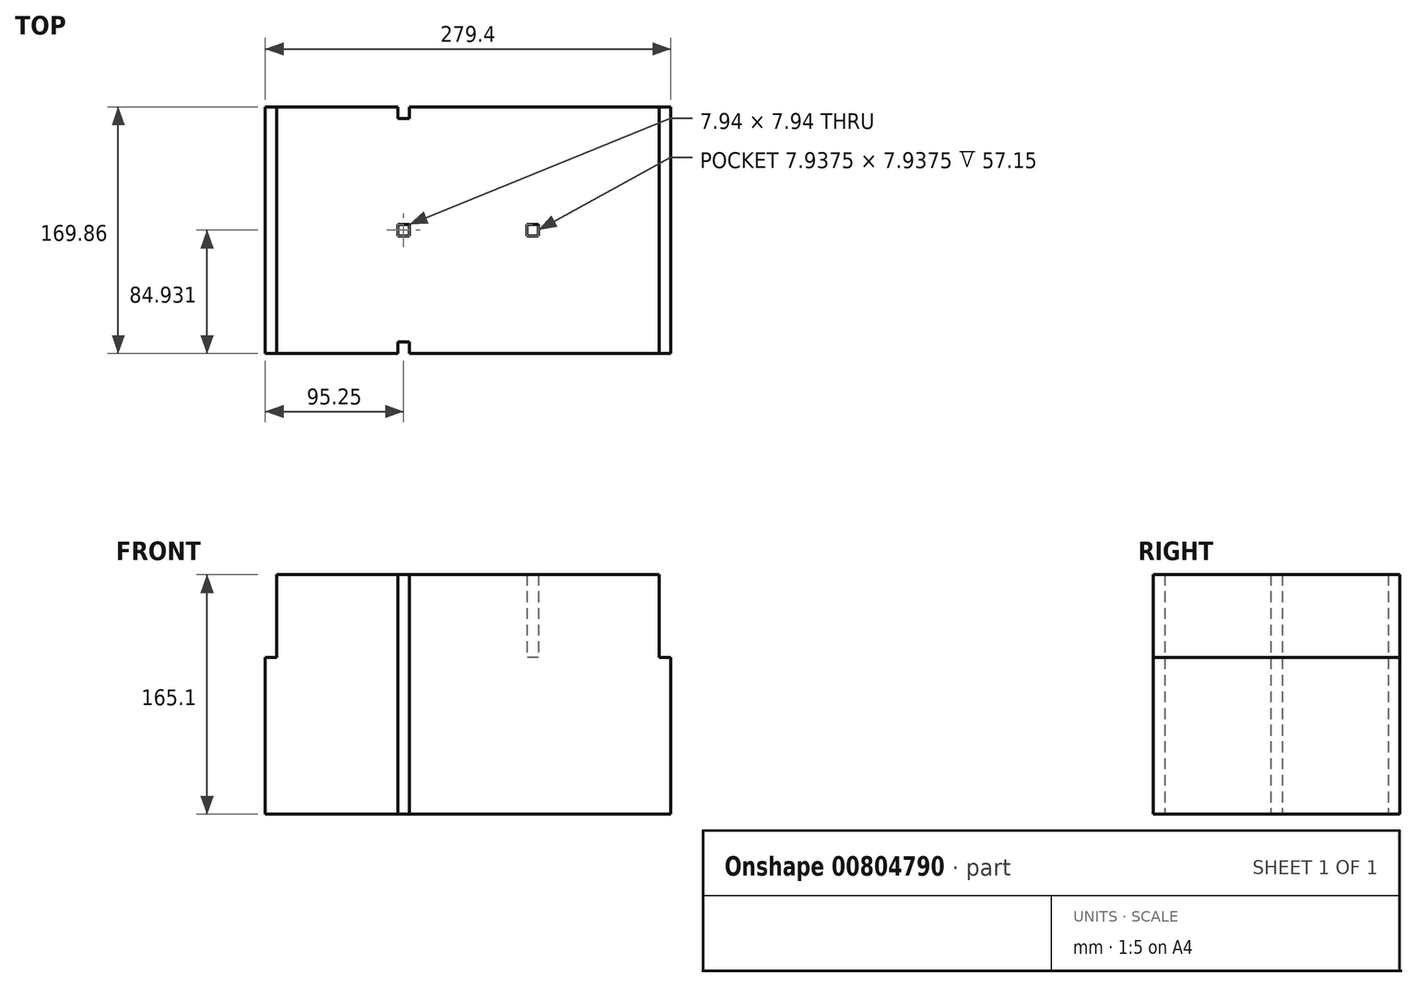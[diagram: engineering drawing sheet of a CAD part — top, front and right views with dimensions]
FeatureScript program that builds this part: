
annotation { "Feature Type Name" : "Feature", "Feature Type Description" : "" }
export const myFeature = defineFeature(function(context is Context, id is Id, definition is map)
    precondition{}
    {
        {
            var Q0;
            Q0=qCreatedBy(makeId("Top.planeOp"),FACE);
            var sketch = newSketch(context, id + "F0", { "sketchPlane" : qUnion([Q0])});
            skLineSegment(sketch, "E0.bottom", {"start": v(-139.7, 0) * mm, "end": v(-44.45, 0) * mm});
            skLineSegment(sketch, "E0.top", {"start": v(-139.7, 88.9) * mm, "end": v(-44.45, 88.9) * mm});
            skLineSegment(sketch, "E0.left", {"start": v(-139.7, 0) * mm, "end": v(-139.7, 88.9) * mm});
            skLineSegment(sketch, "E1.bottom", {"start": v(-44.45, 88.9) * mm, "end": v(44.45, 88.9) * mm});
            skLineSegment(sketch, "E1.top", {"start": v(-44.45, 0) * mm, "end": v(44.45, 0) * mm});
            skLineSegment(sketch, "E2.bottom", {"start": v(44.45, 88.9) * mm, "end": v(139.7, 88.9) * mm});
            skLineSegment(sketch, "E2.top", {"start": v(44.45, 0) * mm, "end": v(139.7, 0) * mm});
            skLineSegment(sketch, "E2.right", {"start": v(139.7, 88.9) * mm, "end": v(139.7, 0) * mm});
            skLineSegment(sketch, "E3", {"start": v(131.76, 88.9) * mm, "end": v(131.76, 0) * mm});
            skLineSegment(sketch, "E4", {"start": v(-131.76, 88.9) * mm, "end": v(-131.76, 0) * mm});
            skLineSegment(sketch, "E5", {"start": v(48.42, 0) * mm, "end": v(48.42, 88.9) * mm});
            skLineSegment(sketch, "E6", {"start": v(-40.48, 88.9) * mm, "end": v(-40.48, 0) * mm});
            skLineSegment(sketch, "E7", {"start": v(-48.42, 88.9) * mm, "end": v(-48.42, 0) * mm});
            skLineSegment(sketch, "E8", {"start": v(40.48, 88.9) * mm, "end": v(40.48, 0) * mm});
            skLineSegment(sketch, "E9.bottom", {"start": v(-139.7, 0) * mm, "end": v(-139.7, 0) * mm});
            skLineSegment(sketch, "E9.top", {"start": v(-139.7, 5.35) * mm, "end": v(-139.7, 5.35) * mm});
            skLineSegment(sketch, "E9.left", {"start": v(-139.7, 0) * mm, "end": v(-139.7, 5.35) * mm});
            skLineSegment(sketch, "E9.right", {"start": v(-139.7, 0) * mm, "end": v(-139.7, 5.35) * mm});
            skLineSegment(sketch, "E10.bottom", {"start": v(139.7, 0) * mm, "end": v(139.7, 0) * mm});
            skLineSegment(sketch, "E10.top", {"start": v(139.7, 7.94) * mm, "end": v(139.7, 7.94) * mm});
            skLineSegment(sketch, "E10.left", {"start": v(139.7, 0) * mm, "end": v(139.7, 7.94) * mm});
            skLineSegment(sketch, "E10.right", {"start": v(139.7, 0) * mm, "end": v(139.7, 7.94) * mm});
            skLineSegment(sketch, "E11.left", {"start": v(139.7, 7.94) * mm, "end": v(139.7, 0) * mm});
            skLineSegment(sketch, "E11.right", {"start": v(139.7, 7.94) * mm, "end": v(139.7, 0) * mm});
            skLineSegment(sketch, "E12.bottom", {"start": v(-139.7, 0) * mm, "end": v(139.7, 0) * mm});
            skLineSegment(sketch, "E12.top", {"start": v(-139.7, 7.94) * mm, "end": v(139.7, 7.94) * mm});
            skLineSegment(sketch, "E12.left", {"start": v(-139.7, 0) * mm, "end": v(-139.7, 7.94) * mm});
            skLineSegment(sketch, "E13.bottom", {"start": v(139.7, 88.9) * mm, "end": v(-139.7, 88.9) * mm});
            skLineSegment(sketch, "E13.top", {"start": v(139.7, 80.96) * mm, "end": v(-139.7, 80.96) * mm});
            skLineSegment(sketch, "E13.left", {"start": v(139.7, 88.9) * mm, "end": v(139.7, 80.96) * mm});
            skLineSegment(sketch, "E13.right", {"start": v(-139.7, 88.9) * mm, "end": v(-139.7, 80.96) * mm});
            skSolve(sketch);
        }
        {
            var Q0;
            {var subQ0=sQuery(id+"F0.wireOp",EDGE,"E13.bottom");var subQ1=sQuery(id+"F0.wireOp",EDGE,"E4");var subQ2=makeQuery(id+"F0.imprint","INTERSECT",VERTEX,{"derivedFrom":[subQ1,subQ0]});Q0=makeQuery(id+"F0.imprint","IMPRINT",FACE,{"disambiguationData":[TD([[makeQuery(id+"F0.imprint","IMPRINT",EDGE,{"disambiguationData":[TD([[subQ2,-1.0]])],"derivedFrom":subQ1}),1.0]])]});}
            var Q1;
            {var subQ0=sQuery(id+"F0.wireOp",EDGE,"E13.bottom");var subQ1=sQuery(id+"F0.wireOp",EDGE,"E6");var subQ2=makeQuery(id+"F0.imprint","INTERSECT",VERTEX,{"derivedFrom":[subQ1,subQ0]});Q1=makeQuery(id+"F0.imprint","IMPRINT",FACE,{"disambiguationData":[TD([[makeQuery(id+"F0.imprint","IMPRINT",EDGE,{"disambiguationData":[TD([[subQ2,-1.0]])],"derivedFrom":subQ1}),1.0]])]});}
            var Q2;
            {var subQ0=sQuery(id+"F0.wireOp",EDGE,"E13.bottom");var subQ1=sQuery(id+"F0.wireOp",EDGE,"E6");var subQ2=makeQuery(id+"F0.imprint","INTERSECT",VERTEX,{"derivedFrom":[subQ1,subQ0]});Q2=makeQuery(id+"F0.imprint","IMPRINT",FACE,{"disambiguationData":[TD([[makeQuery(id+"F0.imprint","IMPRINT",EDGE,{"disambiguationData":[TD([[subQ2,-1.0]])],"derivedFrom":subQ1}),-1.0]])]});}
            var Q3;
            {var subQ5=sQuery(id+"F0.wireOp",EDGE,"E13.right");Q3=makeQuery(id+"F0.imprint","IMPRINT",FACE,{"disambiguationData":[TD([[makeQuery(id+"F0.imprint","IMPRINT",EDGE,{"derivedFrom":subQ5}),1.0]])]});}
            var Q4;
            {var subQ0=sQuery(id+"F0.wireOp",EDGE,"E13.bottom");var subQ1=sQuery(id+"F0.wireOp",EDGE,"E5");var subQ2=makeQuery(id+"F0.imprint","INTERSECT",VERTEX,{"derivedFrom":[subQ1,subQ0]});Q4=makeQuery(id+"F0.imprint","IMPRINT",FACE,{"disambiguationData":[TD([[makeQuery(id+"F0.imprint","IMPRINT",EDGE,{"disambiguationData":[TD([[subQ2,1.0]])],"derivedFrom":subQ1}),1.0]])]});}
            var Q5;
            {var subQ0=sQuery(id+"F0.wireOp",EDGE,"E13.bottom");var subQ1=sQuery(id+"F0.wireOp",EDGE,"E3");var subQ2=makeQuery(id+"F0.imprint","INTERSECT",VERTEX,{"derivedFrom":[subQ1,subQ0]});Q5=makeQuery(id+"F0.imprint","IMPRINT",FACE,{"disambiguationData":[TD([[makeQuery(id+"F0.imprint","IMPRINT",EDGE,{"disambiguationData":[TD([[subQ2,-1.0]])],"derivedFrom":subQ1}),-1.0]])]});}
            var Q6;
            {var subQ5=sQuery(id+"F0.wireOp",EDGE,"E13.left");Q6=makeQuery(id+"F0.imprint","IMPRINT",FACE,{"disambiguationData":[TD([[makeQuery(id+"F0.imprint","IMPRINT",EDGE,{"derivedFrom":subQ5}),-1.0]])]});}
            extrude(context, id + "F1", {"entities" : qUnion([Q0, Q1, Q2, Q3, Q4, Q5, Q6]), "depth" : 165.1 * mm, "offsetDistance" : 25.4 * mm});
        }
        {
            var Q0;
            {var subQ0=sQuery(id+"F0.wireOp",EDGE,"E13.top");var subQ1=sQuery(id+"F0.wireOp",EDGE,"E4");var subQ2=makeQuery(id+"F0.imprint","INTERSECT",VERTEX,{"derivedFrom":[subQ1,subQ0]});Q0=makeQuery(id+"F0.imprint","IMPRINT",FACE,{"disambiguationData":[TD([[makeQuery(id+"F0.imprint","IMPRINT",EDGE,{"disambiguationData":[TD([[subQ2,-1.0]])],"derivedFrom":subQ1}),1.0]])]});}
            var Q1;
            {var subQ0=sQuery(id+"F0.wireOp",EDGE,"E13.top");var subQ1=sQuery(id+"F0.wireOp",EDGE,"E6");var subQ2=makeQuery(id+"F0.imprint","INTERSECT",VERTEX,{"derivedFrom":[subQ1,subQ0]});Q1=makeQuery(id+"F0.imprint","IMPRINT",FACE,{"disambiguationData":[TD([[makeQuery(id+"F0.imprint","IMPRINT",EDGE,{"disambiguationData":[TD([[subQ2,-1.0]])],"derivedFrom":subQ1}),1.0]])]});}
            var Q2;
            {var subQ0=sQuery(id+"F0.wireOp",EDGE,"E13.top");var subQ1=sQuery(id+"F0.wireOp",EDGE,"E3");var subQ2=makeQuery(id+"F0.imprint","INTERSECT",VERTEX,{"derivedFrom":[subQ1,subQ0]});Q2=makeQuery(id+"F0.imprint","IMPRINT",FACE,{"disambiguationData":[TD([[makeQuery(id+"F0.imprint","IMPRINT",EDGE,{"disambiguationData":[TD([[subQ2,-1.0]])],"derivedFrom":subQ1}),-1.0]])]});}
            extrude(context, id + "F2", {"entities" : qUnion([Q0, Q1, Q2]), "depth" : 1.59 * mm, "offsetDistance" : 25.4 * mm});
        }
        {
            var Q0;
            {var subQ3=sQuery(id+"F0.wireOp",EDGE,"E6");Q0=makeQuery(id+"F0.imprint","IMPRINT",FACE,{"disambiguationData":[TD([[makeQuery(id+"F0.imprint","IMPRINT",EDGE,{"derivedFrom":subQ3}),-1.0]])]});}
            var Q1;
            {var subQ3=sQuery(id+"F0.wireOp",EDGE,"E5");Q1=makeQuery(id+"F0.imprint","IMPRINT",FACE,{"disambiguationData":[TD([[makeQuery(id+"F0.imprint","IMPRINT",EDGE,{"derivedFrom":subQ3}),1.0]])]});}
            var Q2;
            {var subQ0=sQuery(id+"F0.wireOp",EDGE,"E2.right");Q2=makeQuery(id+"F0.imprint","IMPRINT",FACE,{"disambiguationData":[TD([[makeQuery(id+"F0.imprint","IMPRINT",EDGE,{"derivedFrom":subQ0}),-1.0]])]});}
            var Q3;
            {var subQ0=sQuery(id+"F0.wireOp",EDGE,"E0.left");Q3=makeQuery(id+"F0.imprint","IMPRINT",FACE,{"disambiguationData":[TD([[makeQuery(id+"F0.imprint","IMPRINT",EDGE,{"derivedFrom":subQ0}),-1.0]])]});}
            var Q4;
            {var subQ0=sQuery(id+"F0.wireOp",EDGE,"E12.bottom");var subQ1=sQuery(id+"F0.wireOp",EDGE,"E4");var subQ2=makeQuery(id+"F0.imprint","INTERSECT",VERTEX,{"derivedFrom":[subQ1,subQ0]});Q4=makeQuery(id+"F0.imprint","IMPRINT",FACE,{"disambiguationData":[TD([[makeQuery(id+"F0.imprint","IMPRINT",EDGE,{"disambiguationData":[TD([[subQ2,1.0]])],"derivedFrom":subQ1}),1.0]])]});}
            var Q5;
            {var subQ0=sQuery(id+"F0.wireOp",EDGE,"E12.bottom");var subQ1=sQuery(id+"F0.wireOp",EDGE,"E4");var subQ2=makeQuery(id+"F0.imprint","INTERSECT",VERTEX,{"derivedFrom":[subQ1,subQ0]});Q5=makeQuery(id+"F0.imprint","IMPRINT",FACE,{"disambiguationData":[TD([[makeQuery(id+"F0.imprint","IMPRINT",EDGE,{"disambiguationData":[TD([[subQ2,1.0]])],"derivedFrom":subQ1}),-1.0]])]});}
            var Q6;
            {var subQ5=sQuery(id+"F0.wireOp",EDGE,"E13.right");Q6=makeQuery(id+"F0.imprint","IMPRINT",FACE,{"disambiguationData":[TD([[makeQuery(id+"F0.imprint","IMPRINT",EDGE,{"derivedFrom":subQ5}),1.0]])]});}
            var Q7;
            {var subQ0=sQuery(id+"F0.wireOp",EDGE,"E13.bottom");var subQ1=sQuery(id+"F0.wireOp",EDGE,"E4");var subQ2=makeQuery(id+"F0.imprint","INTERSECT",VERTEX,{"derivedFrom":[subQ1,subQ0]});Q7=makeQuery(id+"F0.imprint","IMPRINT",FACE,{"disambiguationData":[TD([[makeQuery(id+"F0.imprint","IMPRINT",EDGE,{"disambiguationData":[TD([[subQ2,-1.0]])],"derivedFrom":subQ1}),1.0]])]});}
            var Q8;
            {var subQ0=sQuery(id+"F0.wireOp",EDGE,"E13.bottom");var subQ1=sQuery(id+"F0.wireOp",EDGE,"E6");var subQ2=makeQuery(id+"F0.imprint","INTERSECT",VERTEX,{"derivedFrom":[subQ1,subQ0]});Q8=makeQuery(id+"F0.imprint","IMPRINT",FACE,{"disambiguationData":[TD([[makeQuery(id+"F0.imprint","IMPRINT",EDGE,{"disambiguationData":[TD([[subQ2,-1.0]])],"derivedFrom":subQ1}),1.0]])]});}
            var Q9;
            {var subQ0=sQuery(id+"F0.wireOp",EDGE,"E12.bottom");var subQ1=sQuery(id+"F0.wireOp",EDGE,"E6");var subQ2=makeQuery(id+"F0.imprint","INTERSECT",VERTEX,{"derivedFrom":[subQ1,subQ0]});Q9=makeQuery(id+"F0.imprint","IMPRINT",FACE,{"disambiguationData":[TD([[makeQuery(id+"F0.imprint","IMPRINT",EDGE,{"disambiguationData":[TD([[subQ2,1.0]])],"derivedFrom":subQ1}),1.0]])]});}
            var Q10;
            {var subQ0=sQuery(id+"F0.wireOp",EDGE,"E12.bottom");var subQ1=sQuery(id+"F0.wireOp",EDGE,"E3");var subQ2=makeQuery(id+"F0.imprint","INTERSECT",VERTEX,{"derivedFrom":[subQ1,subQ0]});Q10=makeQuery(id+"F0.imprint","IMPRINT",FACE,{"disambiguationData":[TD([[makeQuery(id+"F0.imprint","IMPRINT",EDGE,{"disambiguationData":[TD([[subQ2,1.0]])],"derivedFrom":subQ1}),-1.0]])]});}
            var Q11;
            {var subQ5=sQuery(id+"F0.wireOp",EDGE,"E10.left");Q11=makeQuery(id+"F0.imprint","IMPRINT",FACE,{"disambiguationData":[TD([[makeQuery(id+"F0.imprint","IMPRINT",EDGE,{"derivedFrom":subQ5}),1.0]])]});}
            var Q12;
            {var subQ5=sQuery(id+"F0.wireOp",EDGE,"E13.left");Q12=makeQuery(id+"F0.imprint","IMPRINT",FACE,{"disambiguationData":[TD([[makeQuery(id+"F0.imprint","IMPRINT",EDGE,{"derivedFrom":subQ5}),-1.0]])]});}
            var Q13;
            {var subQ0=sQuery(id+"F0.wireOp",EDGE,"E13.bottom");var subQ1=sQuery(id+"F0.wireOp",EDGE,"E3");var subQ2=makeQuery(id+"F0.imprint","INTERSECT",VERTEX,{"derivedFrom":[subQ1,subQ0]});Q13=makeQuery(id+"F0.imprint","IMPRINT",FACE,{"disambiguationData":[TD([[makeQuery(id+"F0.imprint","IMPRINT",EDGE,{"disambiguationData":[TD([[subQ2,-1.0]])],"derivedFrom":subQ1}),-1.0]])]});}
            extrude(context, id + "F3", {"entities" : qUnion([Q0, Q1, Q2, Q3, Q4, Q5, Q6, Q7, Q8, Q9, Q10, Q11, Q12, Q13]), "depth" : 107.95 * mm, "offsetDistance" : 25.4 * mm});
        }
        {
            var Q0;
            Q0=makeQuery(id+"F1.opExtrude","SWEPT_BODY",BODY,{"disambiguationData":[OSD([sQuery(id+"F0.wireOp",EDGE,"E13.bottom"),sQuery(id+"F0.wireOp",EDGE,"E13.top"),sQuery(id+"F0.wireOp",EDGE,"E13.left"),sQuery(id+"F0.wireOp",EDGE,"E13.right")])]});
            var Q1;
            Q1=makeQuery(id+"F2.opExtrude","SWEPT_BODY",BODY,{"disambiguationData":[OSD([sQuery(id+"F0.wireOp",EDGE,"E3"),sQuery(id+"F0.wireOp",EDGE,"E5"),sQuery(id+"F0.wireOp",EDGE,"E12.top"),sQuery(id+"F0.wireOp",EDGE,"E13.top")])]});
            var Q2;
            Q2=makeQuery(id+"F2.opExtrude","SWEPT_BODY",BODY,{"disambiguationData":[OSD([sQuery(id+"F0.wireOp",EDGE,"E4"),sQuery(id+"F0.wireOp",EDGE,"E7"),sQuery(id+"F0.wireOp",EDGE,"E12.top"),sQuery(id+"F0.wireOp",EDGE,"E13.top")])]});
            var Q3;
            Q3=makeQuery(id+"F3.opExtrude","SWEPT_BODY",BODY,{"disambiguationData":[OSD([sQuery(id+"F0.wireOp",EDGE,"E0.left"),sQuery(id+"F0.wireOp",EDGE,"E2.right"),sQuery(id+"F0.wireOp",EDGE,"E3"),sQuery(id+"F0.wireOp",EDGE,"E4"),sQuery(id+"F0.wireOp",EDGE,"E5"),sQuery(id+"F0.wireOp",EDGE,"E6"),sQuery(id+"F0.wireOp",EDGE,"E7"),sQuery(id+"F0.wireOp",EDGE,"E8"),sQuery(id+"F0.wireOp",EDGE,"E12.bottom"),sQuery(id+"F0.wireOp",EDGE,"E12.top"),sQuery(id+"F0.wireOp",EDGE,"E12.left"),sQuery(id+"F0.wireOp",EDGE,"E10.left"),sQuery(id+"F0.wireOp",EDGE,"E13.bottom"),sQuery(id+"F0.wireOp",EDGE,"E13.top"),sQuery(id+"F0.wireOp",EDGE,"E13.left"),sQuery(id+"F0.wireOp",EDGE,"E13.right")])]});
            var Q4;
            Q4=makeQuery(id+"F2.opExtrude","SWEPT_BODY",BODY,{"disambiguationData":[OSD([sQuery(id+"F0.wireOp",EDGE,"E6"),sQuery(id+"F0.wireOp",EDGE,"E8"),sQuery(id+"F0.wireOp",EDGE,"E12.top"),sQuery(id+"F0.wireOp",EDGE,"E13.top")])]});
            booleanBodies(context, id + "F4", {"operationType" : BooleanOperationType.UNION, "tools" : qUnion([Q0, Q1, Q2, Q3, Q4])});
        }
        {
            var Q0;
            Q0=qCreatedBy(makeId("Front.planeOp"),FACE);
            cPlane(context, id + "F5", {"entities" : qUnion([Q0]), "cplaneType" : CPlaneType.OFFSET, "offset" : 84.93 * mm, "oppositeDirection" : true, "width" : 152.4 * mm, "height" : 152.4 * mm});
        }
        {
            var Q0;
            Q0=makeQuery(id+"F1.opExtrude","SWEPT_BODY",BODY,{"disambiguationData":[OSD([sQuery(id+"F0.wireOp",EDGE,"E13.bottom"),sQuery(id+"F0.wireOp",EDGE,"E13.top"),sQuery(id+"F0.wireOp",EDGE,"E13.left"),sQuery(id+"F0.wireOp",EDGE,"E13.right")])]});
            var Q1;
            Q1=qCreatedBy(id+"F5.planeOp",FACE);
            mirror(context, id + "F6", {"operationType" : NewBodyOperationType.ADD, "entities" : qUnion([Q0]), "mirrorPlane" : qUnion([Q1])});
        }
    });
